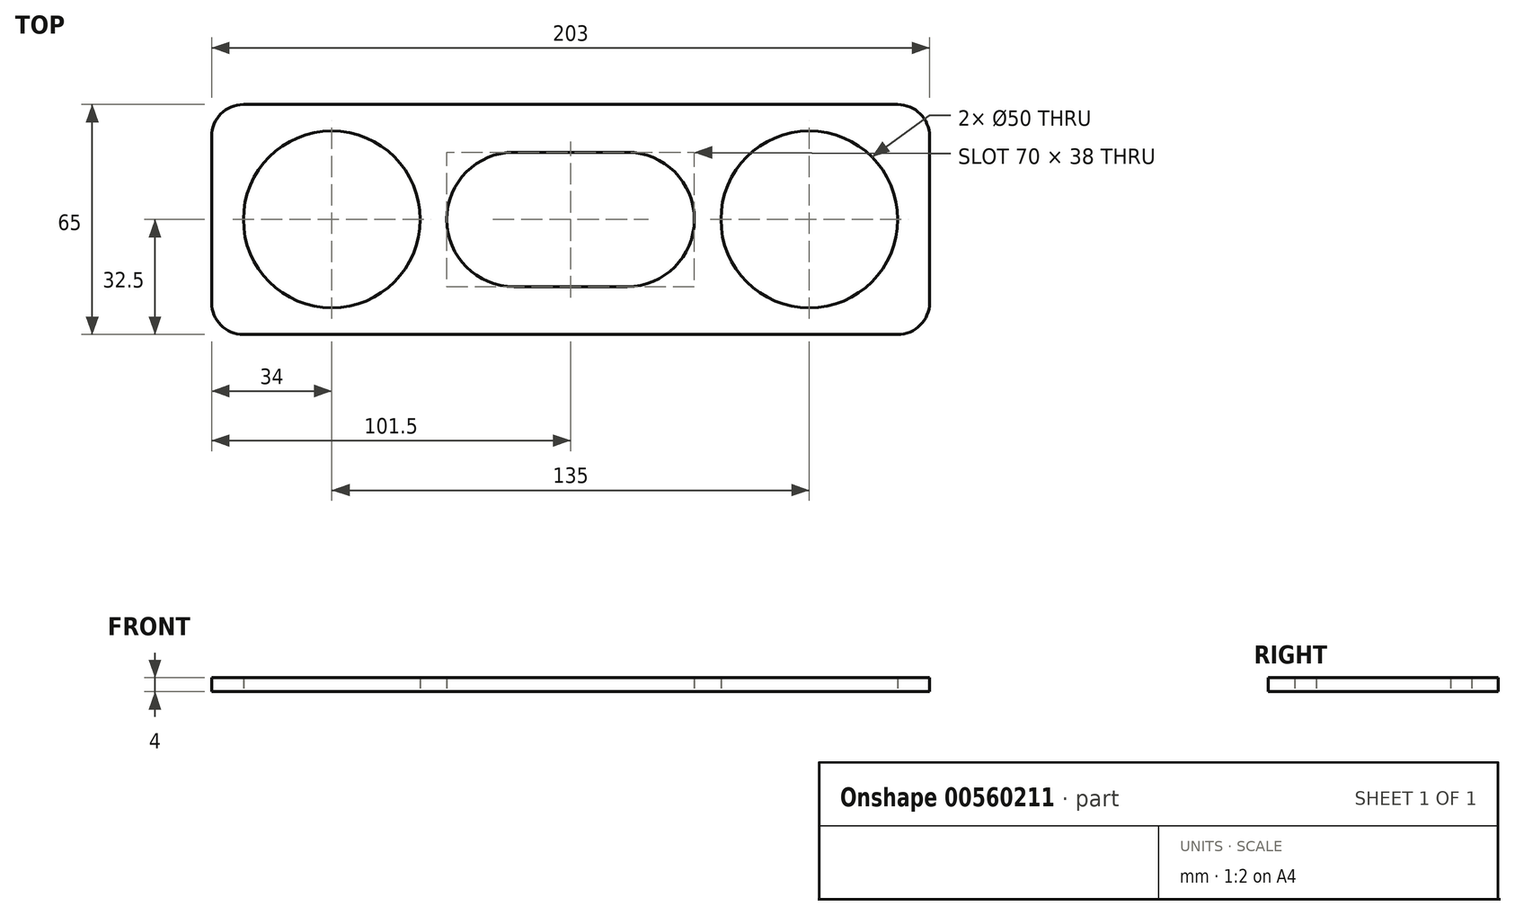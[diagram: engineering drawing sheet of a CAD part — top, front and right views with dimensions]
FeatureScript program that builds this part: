
annotation { "Feature Type Name" : "Feature", "Feature Type Description" : "" }
export const myFeature = defineFeature(function(context is Context, id is Id, definition is map)
    precondition{}
    {
        {
            var Q0;
            Q0=qCreatedBy(makeId("Top.planeOp"),FACE);
            var sketch = newSketch(context, id + "F0", { "sketchPlane" : qUnion([Q0])});
            skLineSegment(sketch, "E0.bottom", {"start": v(92.5, -32.5) * mm, "end": v(-92.5, -32.5) * mm});
            skLineSegment(sketch, "E0.top", {"start": v(92.5, 32.5) * mm, "end": v(-92.5, 32.5) * mm});
            skLineSegment(sketch, "E0.left", {"start": v(101.5, -23.5) * mm, "end": v(101.5, 23.5) * mm});
            skLineSegment(sketch, "E0.right", {"start": v(-101.5, -23.5) * mm, "end": v(-101.5, 23.5) * mm});
            skPoint(sketch, "E1.visualSharp", {"position": v(-101.5, 32.5) * mm});
            skArc(sketch, "E1.filletArc", {"start": v(-92.5, 32.5) * mm, "mid": v(-98.86, 29.86) * mm, "end": v(-101.5, 23.5) * mm});
            skPoint(sketch, "E2.visualSharp", {"position": v(-101.5, -32.5) * mm});
            skArc(sketch, "E2.filletArc", {"start": v(-101.5, -23.5) * mm, "mid": v(-98.86, -29.86) * mm, "end": v(-92.5, -32.5) * mm});
            skPoint(sketch, "E3.visualSharp", {"position": v(101.5, -32.5) * mm});
            skArc(sketch, "E3.filletArc", {"start": v(92.5, -32.5) * mm, "mid": v(98.86, -29.86) * mm, "end": v(101.5, -23.5) * mm});
            skPoint(sketch, "E4.visualSharp", {"position": v(101.5, 32.5) * mm});
            skArc(sketch, "E4.filletArc", {"start": v(101.5, 23.5) * mm, "mid": v(98.86, 29.86) * mm, "end": v(92.5, 32.5) * mm});
            skCircle(sketch, "E5.MirrorC", {"center": v(67.5, 0) * mm, "radius": 25 * mm});
            skCircle(sketch, "E6.MirrorC", {"center": v(-67.5, 0) * mm, "radius": 25 * mm});
            skLineSegment(sketch, "E7.bottom", {"start": v(-16, -19) * mm, "end": v(16, -19) * mm});
            skLineSegment(sketch, "E7.top", {"start": v(-16, 19) * mm, "end": v(16, 19) * mm});
            skPoint(sketch, "E7.middle", {"position": v(0, 0) * mm});
            skArc(sketch, "E8", {"start": v(16, -19) * mm, "mid": v(35, 0) * mm, "end": v(16, 19) * mm});
            skArc(sketch, "E9", {"start": v(-16, 19) * mm, "mid": v(-35, 0) * mm, "end": v(-16, -19) * mm});
            skSolve(sketch);
        }
        {
            var Q0;
            Q0 = qSketchRegion(id + "F0", true);
            extrude(context, id + "F1", {"entities" : qUnion([Q0]), "depth" : 4 * mm, "offsetDistance" : 25 * mm});
        }
    });
